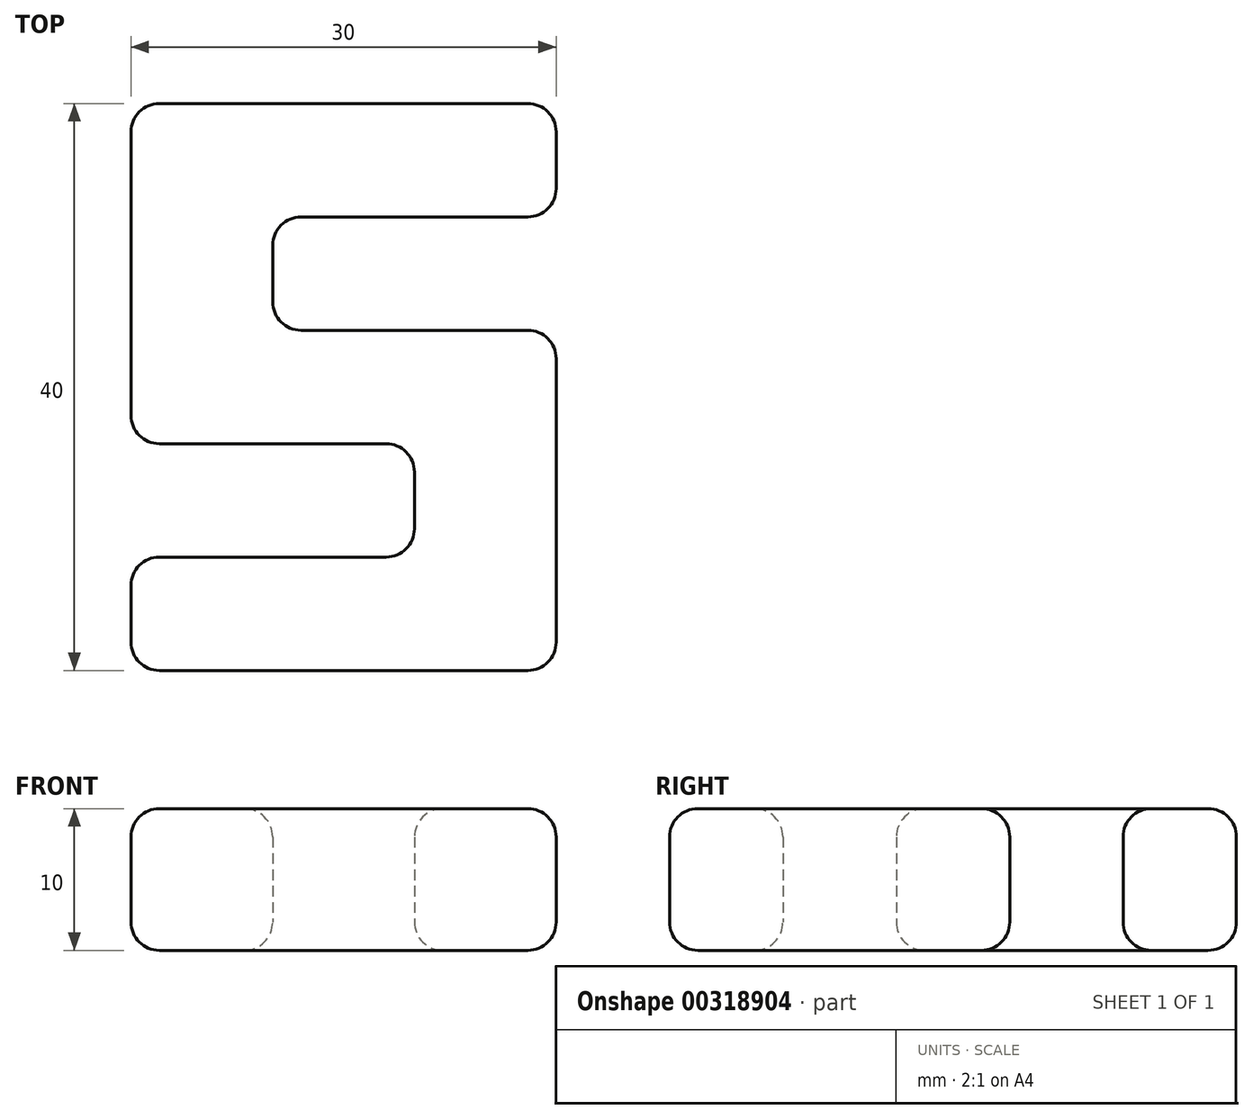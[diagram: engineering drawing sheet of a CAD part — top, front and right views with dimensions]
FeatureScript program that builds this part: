
annotation { "Feature Type Name" : "Feature", "Feature Type Description" : "" }
export const myFeature = defineFeature(function(context is Context, id is Id, definition is map)
    precondition{}
    {
        {
            var Q0;
            Q0=qCreatedBy(makeId("Top.planeOp"),FACE);
            var sketch = newSketch(context, id + "F0", { "sketchPlane" : qUnion([Q0])});
            skLineSegment(sketch, "E0", {"start": v(-30, 0) * mm, "end": v(0, 0) * mm});
            skLineSegment(sketch, "E1", {"start": v(-30, 0) * mm, "end": v(-30, 8) * mm});
            skLineSegment(sketch, "E2", {"start": v(-30, 8) * mm, "end": v(-10, 8) * mm});
            skLineSegment(sketch, "E3", {"start": v(-10, 8) * mm, "end": v(-10, 16) * mm});
            skLineSegment(sketch, "E4", {"start": v(0, 0) * mm, "end": v(0, 24) * mm});
            skLineSegment(sketch, "E5", {"start": v(-10, 16) * mm, "end": v(-30, 16) * mm});
            skLineSegment(sketch, "E6", {"start": v(-30, 16) * mm, "end": v(-30, 13.96) * mm});
            skLineSegment(sketch, "E7", {"start": v(-30, 16) * mm, "end": v(-30, 40) * mm});
            skLineSegment(sketch, "E8", {"start": v(0, 24) * mm, "end": v(-20, 24) * mm});
            skLineSegment(sketch, "E9", {"start": v(-20, 24) * mm, "end": v(-20, 32) * mm});
            skLineSegment(sketch, "E10", {"start": v(-20, 32) * mm, "end": v(0, 32) * mm});
            skLineSegment(sketch, "E11", {"start": v(-30, 40) * mm, "end": v(0, 40) * mm});
            skLineSegment(sketch, "E12", {"start": v(0, 32) * mm, "end": v(0, 40) * mm});
            skSolve(sketch);
        }
        {
            var Q0;
            Q0=makeQuery(id+"F0.imprint","IMPRINT",FACE,{"disambiguationData":[TD([[makeQuery(id+"F0.imprint","IMPRINT",EDGE,{"derivedFrom":sQuery(id+"F0.wireOp",EDGE,"E0")}),1.0]])]});
            extrude(context, id + "F1", {"entities" : qUnion([Q0]), "depth" : 10 * mm});
        }
        {
            var Q0;
            Q0=makeQuery(id+"F1.opExtrude","CAP_FACE",FACE,{"disambiguationData":[OSD([sQuery(id+"F0.wireOp",EDGE,"E0"),sQuery(id+"F0.wireOp",EDGE,"E1"),sQuery(id+"F0.wireOp",EDGE,"E2"),sQuery(id+"F0.wireOp",EDGE,"E3"),sQuery(id+"F0.wireOp",EDGE,"E4"),sQuery(id+"F0.wireOp",EDGE,"E5"),sQuery(id+"F0.wireOp",EDGE,"E7"),sQuery(id+"F0.wireOp",EDGE,"E8"),sQuery(id+"F0.wireOp",EDGE,"E9"),sQuery(id+"F0.wireOp",EDGE,"E10"),sQuery(id+"F0.wireOp",EDGE,"E11"),sQuery(id+"F0.wireOp",EDGE,"E12")])],"isStart":false});
            var Q1;
            Q1=makeQuery(id+"F1.opExtrude","SWEPT_FACE",FACE,{"disambiguationData":[OSD([sQuery(id+"F0.wireOp",EDGE,"E7")])]});
            var Q2;
            Q2=makeQuery(id+"F1.opExtrude","SWEPT_FACE",FACE,{"disambiguationData":[OSD([sQuery(id+"F0.wireOp",EDGE,"E3")])]});
            var Q3;
            Q3=makeQuery(id+"F1.opExtrude","SWEPT_FACE",FACE,{"disambiguationData":[OSD([sQuery(id+"F0.wireOp",EDGE,"E1")])]});
            var Q4;
            Q4=makeQuery(id+"F1.opExtrude","CAP_FACE",FACE,{"disambiguationData":[OSD([sQuery(id+"F0.wireOp",EDGE,"E0"),sQuery(id+"F0.wireOp",EDGE,"E1"),sQuery(id+"F0.wireOp",EDGE,"E2"),sQuery(id+"F0.wireOp",EDGE,"E3"),sQuery(id+"F0.wireOp",EDGE,"E4"),sQuery(id+"F0.wireOp",EDGE,"E5"),sQuery(id+"F0.wireOp",EDGE,"E7"),sQuery(id+"F0.wireOp",EDGE,"E8"),sQuery(id+"F0.wireOp",EDGE,"E9"),sQuery(id+"F0.wireOp",EDGE,"E10"),sQuery(id+"F0.wireOp",EDGE,"E11"),sQuery(id+"F0.wireOp",EDGE,"E12")])],"isStart":true});
            var Q5;
            Q5=makeQuery(id+"F1.opExtrude","SWEPT_FACE",FACE,{"disambiguationData":[OSD([sQuery(id+"F0.wireOp",EDGE,"E11")])]});
            var Q6;
            Q6=makeQuery(id+"F1.opExtrude","SWEPT_FACE",FACE,{"disambiguationData":[OSD([sQuery(id+"F0.wireOp",EDGE,"E4")])]});
            var Q7;
            Q7=makeQuery(id+"F1.opExtrude","SWEPT_FACE",FACE,{"disambiguationData":[OSD([sQuery(id+"F0.wireOp",EDGE,"E9")])]});
            var Q8;
            Q8=makeQuery(id+"F1.opExtrude","SWEPT_FACE",FACE,{"disambiguationData":[OSD([sQuery(id+"F0.wireOp",EDGE,"E12")])]});
            var Q9;
            Q9=makeQuery(id+"F1.opExtrude","CAP_EDGE",EDGE,{"disambiguationData":[OSD([sQuery(id+"F0.wireOp",EDGE,"E7")])],"isStart":true});
            var Q10;
            Q10=makeQuery(id+"F1.opExtrude","CAP_EDGE",EDGE,{"disambiguationData":[OSD([sQuery(id+"F0.wireOp",EDGE,"E11")])],"isStart":true});
            var Q11;
            Q11=makeQuery(id+"F1.opExtrude","CAP_EDGE",EDGE,{"disambiguationData":[OSD([sQuery(id+"F0.wireOp",EDGE,"E8")])],"isStart":true});
            fillet(context, id + "F2", {"entities" : qUnion([Q0, Q1, Q2, Q3, Q4, Q5, Q6, Q7, Q8, Q9, Q10, Q11]), "radius" : 2 * mm, "tangentPropagation" : true, "allowEdgeOverflow" : false});
        }
    });
